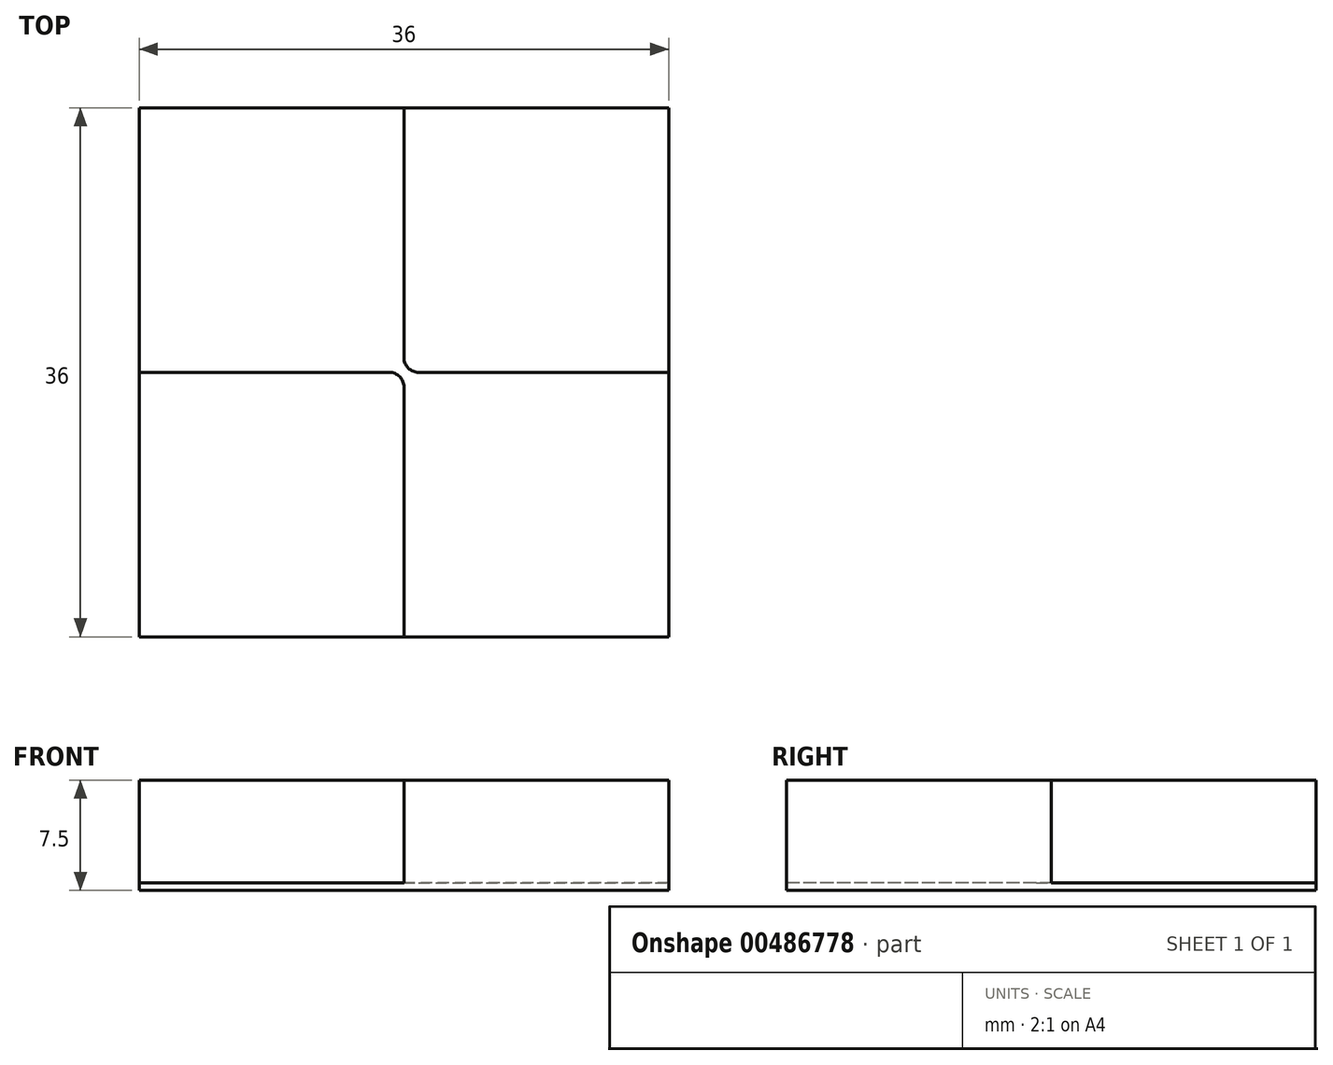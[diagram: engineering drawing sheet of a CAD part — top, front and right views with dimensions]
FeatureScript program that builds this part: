
annotation { "Feature Type Name" : "Feature", "Feature Type Description" : "" }
export const myFeature = defineFeature(function(context is Context, id is Id, definition is map)
    precondition{}
    {
        {
            var Q0;
            Q0=qCreatedBy(makeId("Top.planeOp"),FACE);
            cPlane(context, id + "F0", {"entities" : qUnion([Q0]), "cplaneType" : CPlaneType.OFFSET, "offset" : 7.5 * mm, "width" : 150 * mm, "height" : 150 * mm});
        }
        {
            var Q0;
            Q0=qCreatedBy(id+"F0.planeOp",FACE);
            var sketch = newSketch(context, id + "F1", { "sketchPlane" : qUnion([Q0])});
            skLineSegment(sketch, "E0.bottom", {"start": v(18, 18) * mm, "end": v(-18, 18) * mm});
            skLineSegment(sketch, "E0.top", {"start": v(18, -18) * mm, "end": v(-18, -18) * mm});
            skLineSegment(sketch, "E0.left", {"start": v(18, 18) * mm, "end": v(18, -18) * mm});
            skLineSegment(sketch, "E0.right", {"start": v(-18, 18) * mm, "end": v(-18, -18) * mm});
            skPoint(sketch, "E0.middle", {"position": v(0, 0) * mm});
            skLineSegment(sketch, "E1", {"start": v(-18, 0) * mm, "end": v(18, 0) * mm});
            skLineSegment(sketch, "E2", {"start": v(0, 18) * mm, "end": v(0, -18) * mm});
            skSolve(sketch);
        }
        {
            var Q0;
            {var subQ0=sQuery(id+"F1.wireOp",EDGE,"E0.left");var subQ1=sQuery(id+"F1.wireOp",EDGE,"E0.top");var subQ2=makeQuery(id+"F1.imprint","INTERSECT",VERTEX,{"derivedFrom":[subQ1,subQ0]});Q0=makeQuery(id+"F1.imprint","IMPRINT",FACE,{"disambiguationData":[TD([[makeQuery(id+"F1.imprint","IMPRINT",EDGE,{"disambiguationData":[TD([[subQ2,-1.0]])],"derivedFrom":subQ1}),-1.0]])]});}
            var Q1;
            {var subQ0=sQuery(id+"F1.wireOp",EDGE,"E0.right");var subQ1=sQuery(id+"F1.wireOp",EDGE,"E0.bottom");var subQ2=makeQuery(id+"F1.imprint","INTERSECT",VERTEX,{"derivedFrom":[subQ1,subQ0]});Q1=makeQuery(id+"F1.imprint","IMPRINT",FACE,{"disambiguationData":[TD([[makeQuery(id+"F1.imprint","IMPRINT",EDGE,{"disambiguationData":[TD([[subQ2,1.0]])],"derivedFrom":subQ1}),1.0]])]});}
            var Q2;
            {var subQ0=sQuery(id+"F1.wireOp",EDGE,"E0.left");var subQ1=sQuery(id+"F1.wireOp",EDGE,"E0.bottom");var subQ2=makeQuery(id+"F1.imprint","INTERSECT",VERTEX,{"derivedFrom":[subQ1,subQ0]});Q2=makeQuery(id+"F1.imprint","IMPRINT",FACE,{"disambiguationData":[TD([[makeQuery(id+"F1.imprint","IMPRINT",EDGE,{"disambiguationData":[TD([[subQ2,-1.0]])],"derivedFrom":subQ1}),1.0]])]});}
            var Q3;
            {var subQ0=sQuery(id+"F1.wireOp",EDGE,"E0.right");var subQ1=sQuery(id+"F1.wireOp",EDGE,"E0.top");var subQ2=makeQuery(id+"F1.imprint","INTERSECT",VERTEX,{"derivedFrom":[subQ1,subQ0]});Q3=makeQuery(id+"F1.imprint","IMPRINT",FACE,{"disambiguationData":[TD([[makeQuery(id+"F1.imprint","IMPRINT",EDGE,{"disambiguationData":[TD([[subQ2,1.0]])],"derivedFrom":subQ1}),-1.0]])]});}
            extrude(context, id + "F2", {"entities" : qUnion([Q0, Q1, Q2, Q3]), "oppositeDirection" : true, "depth" : 7.5 * mm, "offsetDistance" : 25 * mm});
        }
        {
            var Q0;
            {var subQ0=sQuery(id+"F1.wireOp",EDGE,"E0.left");var subQ1=sQuery(id+"F1.wireOp",EDGE,"E0.bottom");var subQ2=makeQuery(id+"F1.imprint","INTERSECT",VERTEX,{"derivedFrom":[subQ1,subQ0]});Q0=makeQuery(id+"F1.imprint","IMPRINT",FACE,{"disambiguationData":[TD([[makeQuery(id+"F1.imprint","IMPRINT",EDGE,{"disambiguationData":[TD([[subQ2,-1.0]])],"derivedFrom":subQ1}),1.0]])]});}
            extrude(context, id + "F3", {"entities" : qUnion([Q0]), "operationType" : NewBodyOperationType.REMOVE, "oppositeDirection" : true, "depth" : 7 * mm, "offsetDistance" : 25 * mm});
        }
        {
            var Q0;
            Q0=makeQuery(id+"F3.boolean.opBoolean","COPY",EDGE,{"derivedFrom":makeQuery(id+"F3.opExtrude","SWEPT_EDGE",EDGE,{"disambiguationData":[OSD([sQuery(id+"F1.wireOp",EDGE,"E1"),sQuery(id+"F1.wireOp",EDGE,"E2")])]})});
            fillet(context, id + "F4", {"entities" : qUnion([Q0]), "radius" : 1 * mm, "tangentPropagation" : true, "allowEdgeOverflow" : false});
        }
        {
            var Q0;
            {var subQ0=sQuery(id+"F1.wireOp",EDGE,"E0.right");var subQ1=sQuery(id+"F1.wireOp",EDGE,"E0.top");var subQ2=makeQuery(id+"F1.imprint","INTERSECT",VERTEX,{"derivedFrom":[subQ1,subQ0]});Q0=makeQuery(id+"F1.imprint","IMPRINT",FACE,{"disambiguationData":[TD([[makeQuery(id+"F1.imprint","IMPRINT",EDGE,{"disambiguationData":[TD([[subQ2,1.0]])],"derivedFrom":subQ1}),-1.0]])]});}
            extrude(context, id + "F5", {"entities" : qUnion([Q0]), "operationType" : NewBodyOperationType.REMOVE, "oppositeDirection" : true, "depth" : 7 * mm, "offsetDistance" : 25 * mm});
        }
        {
            var Q0;
            Q0=makeQuery(id+"F5.boolean.opBoolean","COPY",EDGE,{"derivedFrom":makeQuery(id+"F5.opExtrude","SWEPT_EDGE",EDGE,{"disambiguationData":[OSD([sQuery(id+"F1.wireOp",EDGE,"E1"),sQuery(id+"F1.wireOp",EDGE,"E2")])]})});
            fillet(context, id + "F6", {"entities" : qUnion([Q0]), "radius" : 1 * mm, "tangentPropagation" : true, "allowEdgeOverflow" : false});
        }
    });
